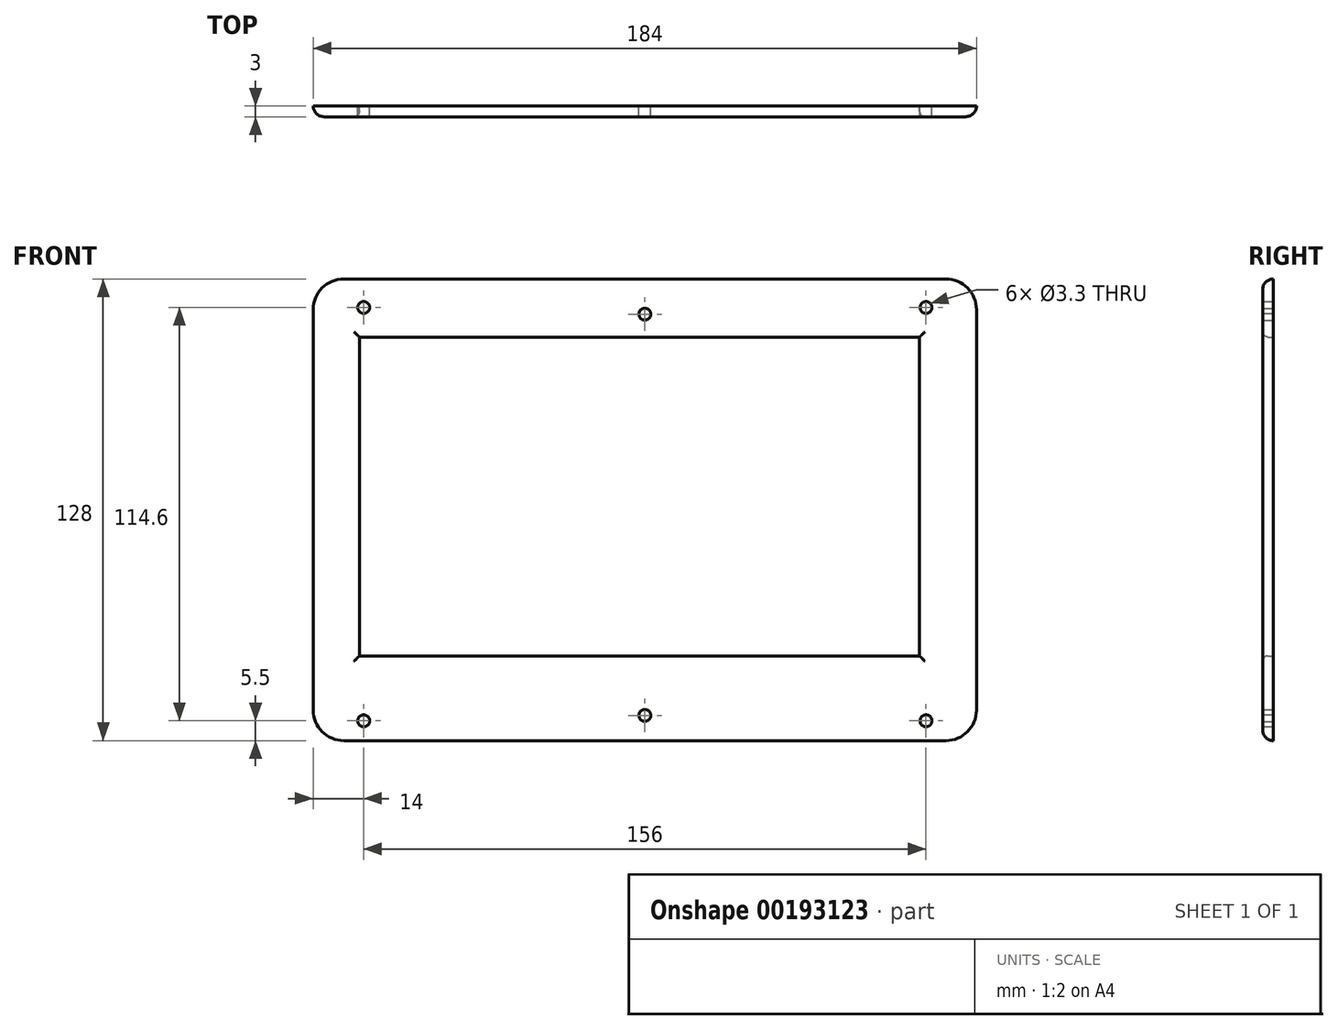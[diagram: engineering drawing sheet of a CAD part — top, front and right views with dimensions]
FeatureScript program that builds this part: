
annotation { "Feature Type Name" : "Feature", "Feature Type Description" : "" }
export const myFeature = defineFeature(function(context is Context, id is Id, definition is map)
    precondition{}
    {
        {
            var Q0;
            Q0=qCreatedBy(makeId("Front.planeOp"),FACE);
            var sketch = newSketch(context, id + "F0", { "sketchPlane" : qUnion([Q0])});
            skLineSegment(sketch, "E0.bottom", {"start": v(-83.5, 64) * mm, "end": v(83.5, 64) * mm});
            skLineSegment(sketch, "E0.top", {"start": v(-83.5, -64) * mm, "end": v(83.5, -64) * mm});
            skLineSegment(sketch, "E0.left", {"start": v(-92, 55.5) * mm, "end": v(-92, -55.5) * mm});
            skLineSegment(sketch, "E0.right", {"start": v(92, 55.5) * mm, "end": v(92, -55.5) * mm});
            skPoint(sketch, "E0.middle", {"position": v(0, 0) * mm});
            skPoint(sketch, "E1.visualSharp", {"position": v(-92, 64) * mm});
            skArc(sketch, "E1.filletArc", {"start": v(-83.5, 64) * mm, "mid": v(-89.51, 61.51) * mm, "end": v(-92, 55.5) * mm});
            skPoint(sketch, "E2.visualSharp", {"position": v(92, 64) * mm});
            skArc(sketch, "E2.filletArc", {"start": v(92, 55.5) * mm, "mid": v(89.51, 61.51) * mm, "end": v(83.5, 64) * mm});
            skPoint(sketch, "E3.visualSharp", {"position": v(-92, -64) * mm});
            skArc(sketch, "E3.filletArc", {"start": v(-92, -55.5) * mm, "mid": v(-89.51, -61.51) * mm, "end": v(-83.5, -64) * mm});
            skPoint(sketch, "E4.visualSharp", {"position": v(92, -64) * mm});
            skArc(sketch, "E4.filletArc", {"start": v(83.5, -64) * mm, "mid": v(89.51, -61.51) * mm, "end": v(92, -55.5) * mm});
            skLineSegment(sketch, "E5.bottom", {"start": v(-83.5, 52.5) * mm, "end": v(83.5, 52.5) * mm});
            skLineSegment(sketch, "E5.top", {"start": v(-83.5, -50.5) * mm, "end": v(45.5, -50.5) * mm});
            skLineSegment(sketch, "E5.left", {"start": v(-83.5, 52.5) * mm, "end": v(-83.5, -50.5) * mm});
            skLineSegment(sketch, "E5.right", {"start": v(83.5, 52.5) * mm, "end": v(83.5, -51.5) * mm});
            skLineSegment(sketch, "E6", {"start": v(46.5, -51.5) * mm, "end": v(46.5, -51.5) * mm});
            skLineSegment(sketch, "E7", {"start": v(47.5, -52.5) * mm, "end": v(82.5, -52.5) * mm});
            skPoint(sketch, "E8.visualSharp", {"position": v(46.5, -50.5) * mm});
            skArc(sketch, "E8.filletArc", {"start": v(46.5, -51.5) * mm, "mid": v(46.2, -50.8) * mm, "end": v(45.5, -50.5) * mm});
            skPoint(sketch, "E9.visualSharp", {"position": v(46.5, -52.5) * mm});
            skArc(sketch, "E9.filletArc", {"start": v(46.5, -51.5) * mm, "mid": v(46.8, -52.2) * mm, "end": v(47.5, -52.5) * mm});
            skPoint(sketch, "E10.visualSharp", {"position": v(83.5, -52.5) * mm});
            skArc(sketch, "E10.filletArc", {"start": v(82.5, -52.5) * mm, "mid": v(83.2, -52.2) * mm, "end": v(83.5, -51.5) * mm});
            skLineSegment(sketch, "E11.bottom", {"start": v(-79.2, 47.9) * mm, "end": v(76.2, 47.9) * mm});
            skLineSegment(sketch, "E11.top", {"start": v(-79.2, -40.5) * mm, "end": v(76.2, -40.5) * mm});
            skLineSegment(sketch, "E11.left", {"start": v(-79.2, 47.9) * mm, "end": v(-79.2, -40.5) * mm});
            skLineSegment(sketch, "E11.right", {"start": v(76.2, 47.9) * mm, "end": v(76.2, -40.5) * mm});
            skCircle(sketch, "E12", {"center": v(-78, 56.1) * mm, "radius": 1.65 * mm});
            skCircle(sketch, "E13", {"center": v(78, 56.1) * mm, "radius": 1.65 * mm});
            skCircle(sketch, "E14", {"center": v(0, 54.25) * mm, "radius": 1.65 * mm});
            skPoint(sketch, "E15", {"position": v(0, 52.5) * mm});
            skCircle(sketch, "E16", {"center": v(-78, -58.5) * mm, "radius": 1.65 * mm});
            skCircle(sketch, "E17", {"center": v(0, -57) * mm, "radius": 1.65 * mm});
            skCircle(sketch, "E18", {"center": v(78, -58.5) * mm, "radius": 1.65 * mm});
            skSolve(sketch);
        }
        {
            var Q0;
            Q0=makeQuery(id+"F0.imprint","IMPRINT",FACE,{"disambiguationData":[TD([[makeQuery(id+"F0.imprint","IMPRINT",EDGE,{"derivedFrom":sQuery(id+"F0.wireOp",EDGE,"E0.bottom")}),-1.0]])]});
            var Q1;
            Q1=makeQuery(id+"F0.imprint","IMPRINT",FACE,{"disambiguationData":[TD([[makeQuery(id+"F0.imprint","IMPRINT",EDGE,{"derivedFrom":sQuery(id+"F0.wireOp",EDGE,"E5.bottom")}),-1.0]])]});
            extrude(context, id + "F1", {"entities" : qUnion([Q0, Q1]), "depth" : 3 * mm});
        }
        {
            var Q0;
            Q0=makeQuery(id+"F1.opExtrude","CAP_EDGE",EDGE,{"disambiguationData":[OSD([sQuery(id+"F0.wireOp",EDGE,"E0.right")])],"isStart":false});
            fillet(context, id + "F2", {"entities" : qUnion([Q0]), "radius" : 3 * mm, "tangentPropagation" : true, "allowEdgeOverflow" : false});
        }
        {
            var Q0;
            Q0=makeQuery(id+"F1.opExtrude","CAP_EDGE",EDGE,{"disambiguationData":[OSD([sQuery(id+"F0.wireOp",EDGE,"E11.left")])],"isStart":false});
            var Q1;
            Q1=makeQuery(id+"F1.opExtrude","CAP_EDGE",EDGE,{"disambiguationData":[OSD([sQuery(id+"F0.wireOp",EDGE,"E11.bottom")])],"isStart":false});
            var Q2;
            Q2=makeQuery(id+"F1.opExtrude","CAP_EDGE",EDGE,{"disambiguationData":[OSD([sQuery(id+"F0.wireOp",EDGE,"E11.right")])],"isStart":false});
            var Q3;
            Q3=makeQuery(id+"F1.opExtrude","CAP_EDGE",EDGE,{"disambiguationData":[OSD([sQuery(id+"F0.wireOp",EDGE,"E11.top")])],"isStart":false});
            fillet(context, id + "F3", {"entities" : qUnion([Q0, Q1, Q2, Q3]), "radius" : 1.5 * mm, "tangentPropagation" : true, "allowEdgeOverflow" : false});
        }
    });
